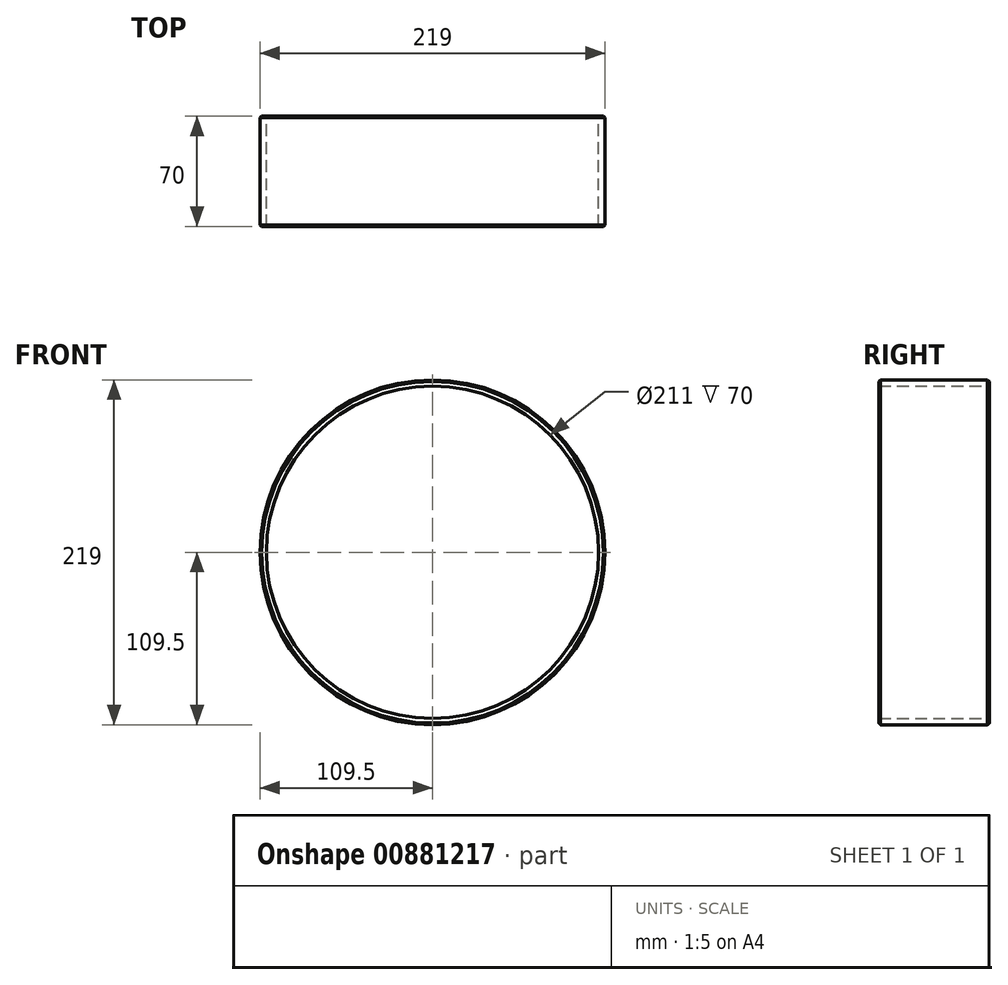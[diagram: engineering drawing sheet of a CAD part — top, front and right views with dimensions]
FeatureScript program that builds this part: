
annotation { "Feature Type Name" : "Feature", "Feature Type Description" : "" }
export const myFeature = defineFeature(function(context is Context, id is Id, definition is map)
    precondition{}
    {
        {
            var Q0;
            Q0=qCreatedBy(makeId("Front.planeOp"),FACE);
            var sketch = newSketch(context, id + "F0", { "sketchPlane" : qUnion([Q0])});
            skCircle(sketch, "E0", {"center": v(0, 0) * mm, "radius": 105.5 * mm});
            skCircle(sketch, "E1", {"center": v(0, 0) * mm, "radius": 109.5 * mm});
            skSolve(sketch);
        }
        {
            var Q0;
            Q0 = qSketchRegion(id + "F0", true);
            extrude(context, id + "F1", {"entities" : qUnion([Q0]), "depth" : 70 * mm, "offsetDistance" : 25 * mm});
        }
        {
            var Q0;
            Q0=makeQuery(id+"F1.opExtrude","CAP_EDGE",EDGE,{"disambiguationData":[OSD([sQuery(id+"F0.wireOp",EDGE,"E1")])],"isStart":false});
            var Q1;
            Q1=makeQuery(id+"F1.opExtrude","CAP_EDGE",EDGE,{"disambiguationData":[OSD([sQuery(id+"F0.wireOp",EDGE,"E1")])],"isStart":true});
            chamfer(context, id + "F2", {"entities" : qUnion([Q0, Q1]), "width" : 1 * mm, "tangentPropagation" : true});
        }
    });
